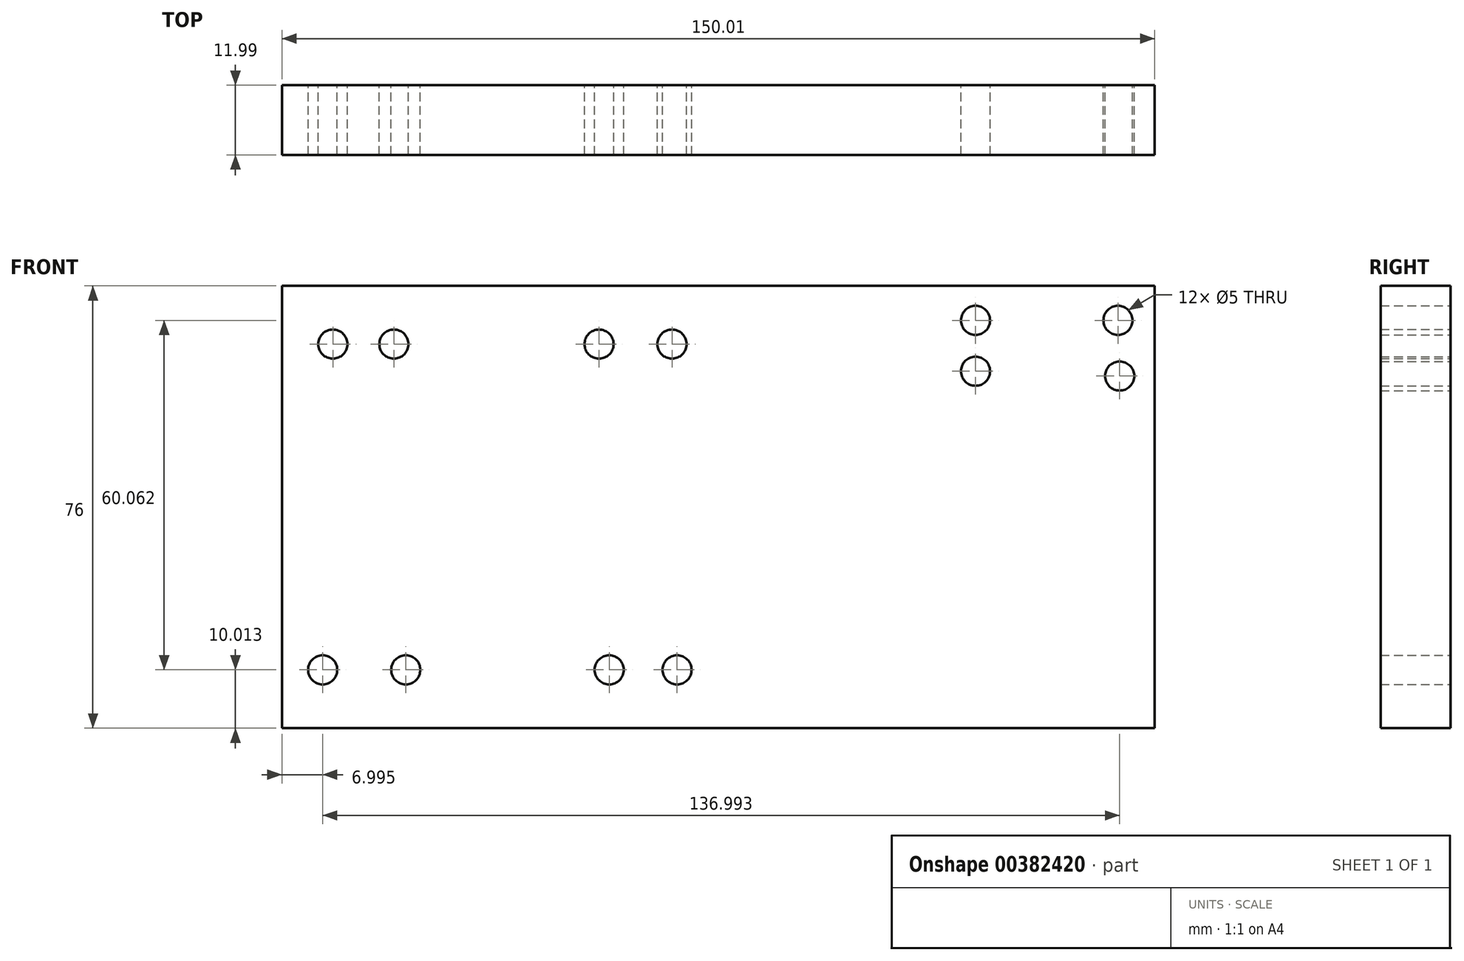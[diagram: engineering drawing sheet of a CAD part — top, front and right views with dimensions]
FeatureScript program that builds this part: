
annotation { "Feature Type Name" : "Feature", "Feature Type Description" : "" }
export const myFeature = defineFeature(function(context is Context, id is Id, definition is map)
    precondition{}
    {
        {
            var Q0;
            Q0=qCreatedBy(makeId("Front.planeOp"),FACE);
            var sketch = newSketch(context, id + "F0", { "sketchPlane" : qUnion([Q0])});
            skLineSegment(sketch, "E0.bottom", {"start": v(-75.2, 35.51) * mm, "end": v(74.81, 35.51) * mm});
            skLineSegment(sketch, "E0.top", {"start": v(-75.2, -40.49) * mm, "end": v(74.81, -40.49) * mm});
            skLineSegment(sketch, "E0.left", {"start": v(-75.2, 35.51) * mm, "end": v(-75.2, -40.49) * mm});
            skLineSegment(sketch, "E0.right", {"start": v(74.81, 35.51) * mm, "end": v(74.81, -40.49) * mm});
            skCircle(sketch, "E1", {"center": v(-7.29, -30.48) * mm, "radius": 2.5 * mm});
            skCircle(sketch, "E2", {"center": v(-18.95, -30.48) * mm, "radius": 2.5 * mm});
            skCircle(sketch, "E3", {"center": v(-53.92, -30.48) * mm, "radius": 2.5 * mm});
            skCircle(sketch, "E4", {"center": v(-68.2, -30.48) * mm, "radius": 2.5 * mm});
            skCircle(sketch, "E5", {"center": v(-66.46, 25.5) * mm, "radius": 2.5 * mm});
            skCircle(sketch, "E6", {"center": v(-55.96, 25.5) * mm, "radius": 2.5 * mm});
            skCircle(sketch, "E7", {"center": v(-20.7, 25.5) * mm, "radius": 2.5 * mm});
            skCircle(sketch, "E8", {"center": v(-8.16, 25.5) * mm, "radius": 2.5 * mm});
            skCircle(sketch, "E9", {"center": v(44.01, 29.58) * mm, "radius": 2.5 * mm});
            skCircle(sketch, "E10", {"center": v(68.5, 29.58) * mm, "radius": 2.5 * mm});
            skCircle(sketch, "E11", {"center": v(68.79, 20.02) * mm, "radius": 2.5 * mm});
            skCircle(sketch, "E12", {"center": v(44.01, 20.84) * mm, "radius": 2.5 * mm});
            skSolve(sketch);
        }
        {
            var Q0;
            Q0=makeQuery(id+"F0.imprint","IMPRINT",FACE,{"disambiguationData":[TD([[makeQuery(id+"F0.imprint","IMPRINT",EDGE,{"derivedFrom":sQuery(id+"F0.wireOp",EDGE,"E0.bottom")}),-1.0]])]});
            extrude(context, id + "F1", {"entities" : qUnion([Q0]), "depth" : 12 * mm});
        }
    });
